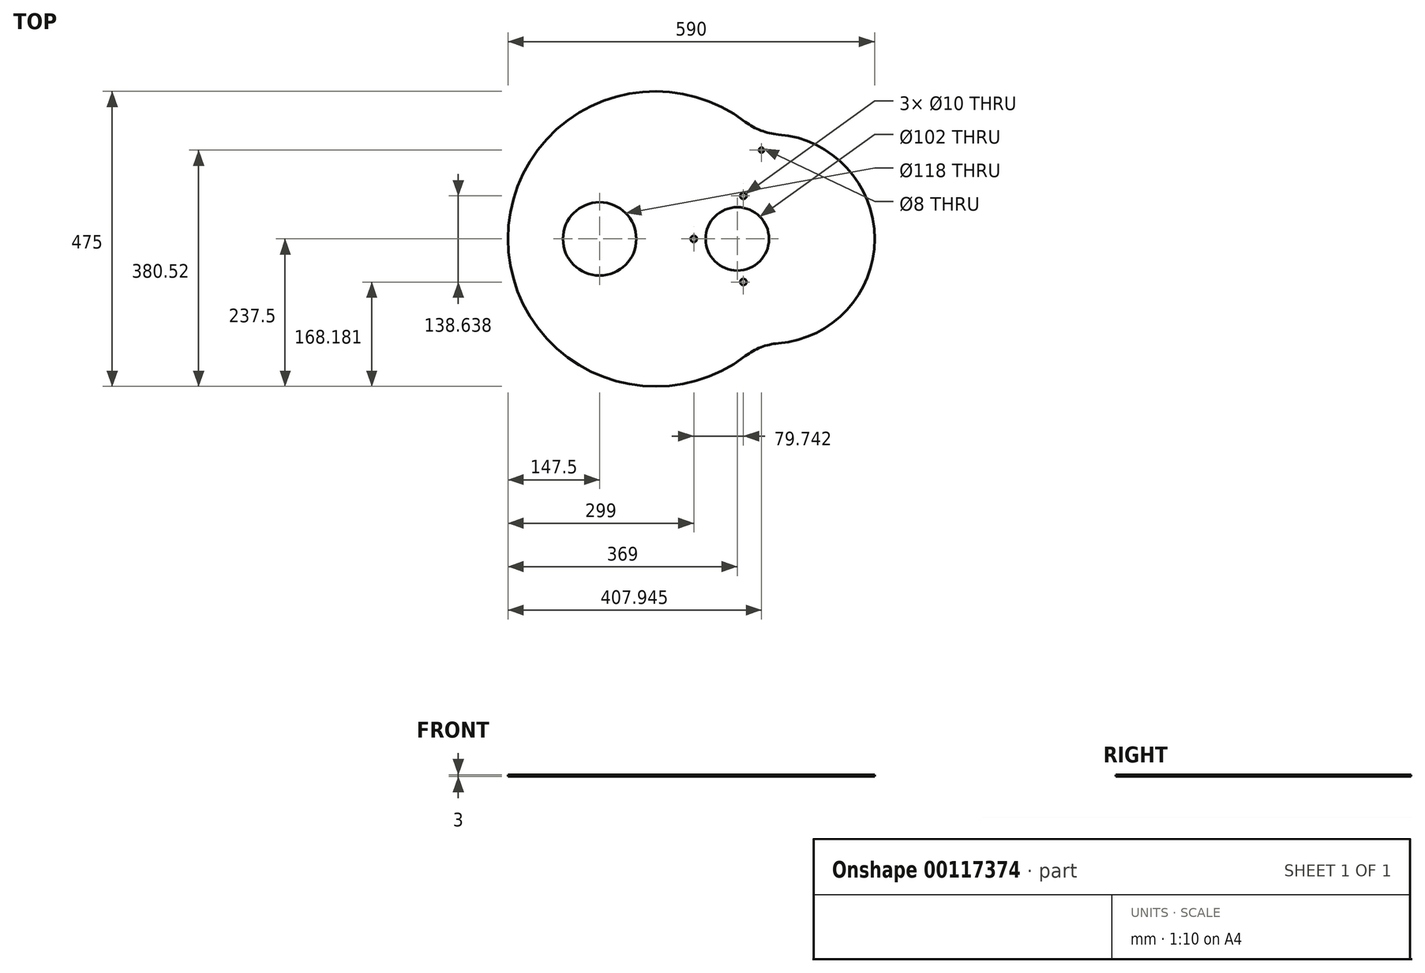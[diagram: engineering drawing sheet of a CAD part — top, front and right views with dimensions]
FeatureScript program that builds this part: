
annotation { "Feature Type Name" : "Feature", "Feature Type Description" : "" }
export const myFeature = defineFeature(function(context is Context, id is Id, definition is map)
    precondition{}
    {
        {
            var Q0;
            Q0=qCreatedBy(makeId("Top.planeOp"),FACE);
            var sketch = newSketch(context, id + "F0", { "sketchPlane" : qUnion([Q0])});
            skLineSegment(sketch, "E0", {"start": v(0, 0) * mm, "end": v(237.5, 0) * mm, "construction": true});
            skCircle(sketch, "E1", {"center": v(131.5, 0) * mm, "radius": 51 * mm});
            skCircle(sketch, "E2.0", {"center": v(131.5, 0) * mm, "radius": 70 * mm, "construction": true});
            skLineSegment(sketch, "E3", {"start": v(131.5, 0) * mm, "end": v(141.24, 69.32) * mm, "construction": true});
            skCircle(sketch, "E4.0", {"center": v(0, 0) * mm, "radius": 222.5 * mm, "construction": true});
            skLineSegment(sketch, "E5", {"start": v(237.5, 0) * mm, "end": v(352.5, 0) * mm, "construction": true});
            skArc(sketch, "E6", {"start": v(352.5, 0) * mm, "mid": v(297.34, 124.77) * mm, "end": v(167.94, 167.94) * mm});
            skLineSegment(sketch, "E7", {"start": v(0, 0) * mm, "end": v(167.94, 167.94) * mm, "construction": true});
            skArc(sketch, "E8.MirrorCS", {"start": v(352.5, 0) * mm, "mid": v(297.34, -124.77) * mm, "end": v(167.94, -167.94) * mm});
            skArc(sketch, "E9", {"start": v(167.94, 167.94) * mm, "mid": v(-237.5, 0) * mm, "end": v(167.94, -167.94) * mm});
            skArc(sketch, "E10", {"start": v(167.94, -167.94) * mm, "mid": v(237.5, 0) * mm, "end": v(167.94, 167.94) * mm, "construction": true});
            skCircle(sketch, "E11", {"center": v(-90, 0) * mm, "radius": 59 * mm});
            skLineSegment(sketch, "E12", {"start": v(0, 0) * mm, "end": v(-90, 0) * mm, "construction": true});
            skPoint(sketch, "E13", {"position": v(182.5, 0) * mm});
            skLineSegment(sketch, "E14", {"start": v(382.5, 252.8) * mm, "end": v(382.5, -235.2) * mm, "construction": true});
            skLineSegment(sketch, "E15", {"start": v(0, 0) * mm, "end": v(170.44, 143.02) * mm, "construction": true});
            skPoint(sketch, "E16", {"position": v(61.5, 0) * mm});
            skPoint(sketch, "E17", {"position": v(141.24, -69.32) * mm});
            skSolve(sketch);
        }
        {
            var Q0;
            Q0=qSketchRegion(id+"F0",true);
            extrude(context, id + "F1", {"entities" : qUnion([Q0]), "depth" : 3 * mm});
        }
        {
            var Q0;
            Q0=makeQuery(id+"F1.opExtrude","SWEPT_EDGE",EDGE,{"disambiguationData":[OSD([sQuery(id+"F0.wireOp",EDGE,"E8.MirrorCS"),sQuery(id+"F0.wireOp",EDGE,"E9")])]});
            var Q1;
            Q1=makeQuery(id+"F1.opExtrude","SWEPT_EDGE",EDGE,{"disambiguationData":[OSD([sQuery(id+"F0.wireOp",EDGE,"E6"),sQuery(id+"F0.wireOp",EDGE,"E9")])]});
            fillet(context, id + "F2", {"entities" : qUnion([Q0, Q1]), "radius" : 100 * mm, "tangentPropagation" : true, "allowEdgeOverflow" : false});
        }
        {
            var Q0;
            Q0=sQuery(id+"F0.wireOp",VERTEX,"E15.end");
            var Q1;
            Q1=makeQuery(id+"F1.opExtrude","SWEPT_BODY",BODY,{"disambiguationData":[OSD([sQuery(id+"F0.wireOp",EDGE,"E1"),sQuery(id+"F0.wireOp",EDGE,"RPsCepcg-DvIT-TJ4T-KVvD-yfufvOwV1Lhv"),sQuery(id+"F0.wireOp",EDGE,"x3hxcPYF-bFqp-voUk-DmIt-QCUFP6n3AsHw"),sQuery(id+"F0.wireOp",EDGE,"259c4eee-24ee-4c9b-a876-d044885e4a360.MirrorC"),sQuery(id+"F0.wireOp",EDGE,"E6"),sQuery(id+"F0.wireOp",EDGE,"E8.MirrorCS"),sQuery(id+"F0.wireOp",EDGE,"E9"),sQuery(id+"F0.wireOp",EDGE,"E11")])]});
            hole(context, id + "F3", {"style" : HoleStyle.SIMPLE, "endStyle" : HoleEndStyle.THROUGH, "oppositeDirection" : true, "holeDiameter" : 8 * mm, "tappedDepth" : 12 * mm, "tapClearance" : 3, "locations" : qUnion([Q0]), "scope" : qUnion([Q1])});
        }
        {
            var Q0;
            Q0=sQuery(id+"F0.wireOp",VERTEX,"E3.end");
            var Q1;
            Q1=sQuery(id+"F0.wireOp",VERTEX,"E16");
            var Q2;
            Q2=sQuery(id+"F0.wireOp",VERTEX,"E17");
            var Q3;
            Q3=makeQuery(id+"F1.opExtrude","SWEPT_BODY",BODY,{"disambiguationData":[OSD([sQuery(id+"F0.wireOp",EDGE,"E1"),sQuery(id+"F0.wireOp",EDGE,"E6"),sQuery(id+"F0.wireOp",EDGE,"E8.MirrorCS"),sQuery(id+"F0.wireOp",EDGE,"E9"),sQuery(id+"F0.wireOp",EDGE,"E11")])]});
            hole(context, id + "F4", {"style" : HoleStyle.SIMPLE, "endStyle" : HoleEndStyle.THROUGH, "oppositeDirection" : true, "holeDiameter" : 10 * mm, "tappedDepth" : 12 * mm, "tapClearance" : 3, "locations" : qUnion([Q0, Q1, Q2]), "scope" : qUnion([Q3])});
        }
        {
            var Q0;
            Q0=qCreatedBy(makeId("Top.planeOp"),FACE);
            cPlane(context, id + "F5", {"entities" : qUnion([Q0]), "cplaneType" : CPlaneType.OFFSET, "offset" : 25 * mm, "oppositeDirection" : true, "width" : 150 * mm, "height" : 150 * mm});
        }
    });
